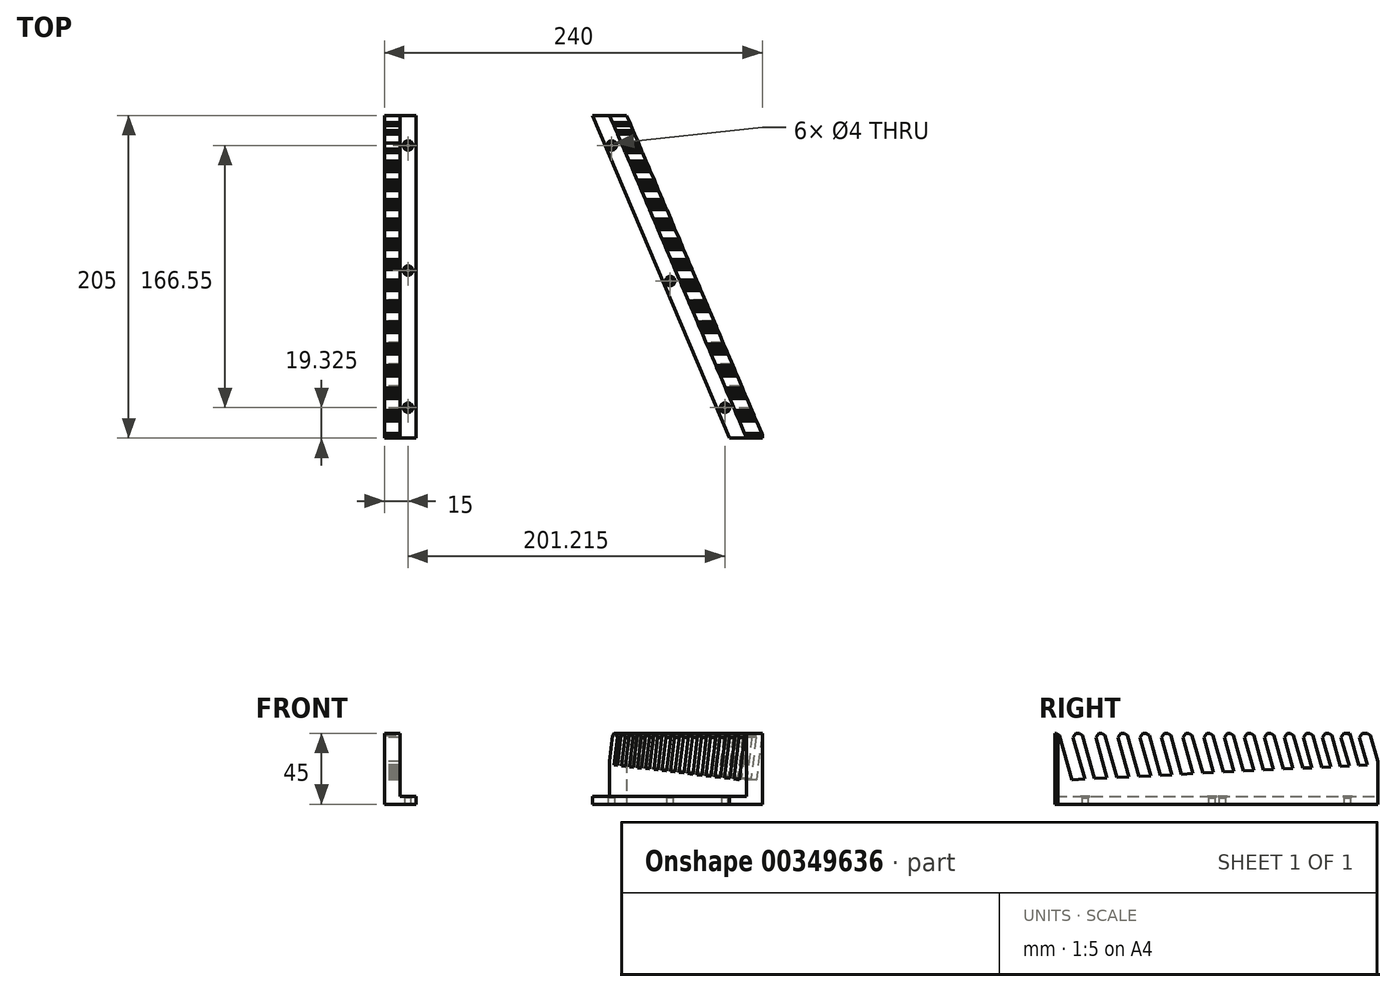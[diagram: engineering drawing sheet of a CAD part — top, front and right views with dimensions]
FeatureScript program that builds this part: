
annotation { "Feature Type Name" : "Feature", "Feature Type Description" : "" }
export const myFeature = defineFeature(function(context is Context, id is Id, definition is map)
    precondition{}
    {
        {
            var Q0;
            Q0=qCreatedBy(makeId("Right.planeOp"),FACE);
            var sketch = newSketch(context, id + "F0", { "sketchPlane" : qUnion([Q0])});
            skLineSegment(sketch, "E0.bottom", {"start": v(0, 0) * mm, "end": v(200, 0) * mm});
            skLineSegment(sketch, "E0.top", {"start": v(0, 45) * mm, "end": v(2.54, 45) * mm});
            skLineSegment(sketch, "E0.left", {"start": v(0, 0) * mm, "end": v(0, 45) * mm});
            skLineSegment(sketch, "E1", {"start": v(198.34, 24.92) * mm, "end": v(193.01, 24.65) * mm});
            skLineSegment(sketch, "E2", {"start": v(2.54, 45) * mm, "end": v(10.85, 15.54) * mm});
            skLineSegment(sketch, "E3", {"start": v(10.85, 45) * mm, "end": v(19.05, 15.95) * mm});
            skLineSegment(sketch, "E4", {"start": v(17.09, 45) * mm, "end": v(25.2, 16.26) * mm});
            skLineSegment(sketch, "E5", {"start": v(25.2, 45) * mm, "end": v(33.3, 16.26) * mm});
            skLineSegment(sketch, "E6", {"start": v(31.43, 45) * mm, "end": v(39.33, 16.97) * mm});
            skLineSegment(sketch, "E7", {"start": v(39.32, 45) * mm, "end": v(47.12, 17.36) * mm});
            skLineSegment(sketch, "E8", {"start": v(45.56, 45) * mm, "end": v(53.27, 17.66) * mm});
            skLineSegment(sketch, "E9", {"start": v(53.25, 45) * mm, "end": v(60.85, 18.04) * mm});
            skLineSegment(sketch, "E10", {"start": v(59.48, 45) * mm, "end": v(67, 18.35) * mm});
            skLineSegment(sketch, "E11", {"start": v(66.96, 45) * mm, "end": v(74.37, 18.72) * mm});
            skLineSegment(sketch, "E12", {"start": v(73.2, 45) * mm, "end": v(80.52, 19.03) * mm});
            skLineSegment(sketch, "E13", {"start": v(80.47, 45) * mm, "end": v(87.69, 19.38) * mm});
            skLineSegment(sketch, "E14", {"start": v(86.7, 45) * mm, "end": v(93.84, 19.7) * mm});
            skLineSegment(sketch, "E15", {"start": v(93.77, 45) * mm, "end": v(100.8, 20.04) * mm});
            skLineSegment(sketch, "E16", {"start": v(100, 45) * mm, "end": v(106.95, 20.35) * mm});
            skLineSegment(sketch, "E17", {"start": v(106.86, 45) * mm, "end": v(113.71, 20.69) * mm});
            skLineSegment(sketch, "E18", {"start": v(113.1, 45) * mm, "end": v(119.86, 21) * mm});
            skLineSegment(sketch, "E19", {"start": v(119.74, 45) * mm, "end": v(126.42, 21.32) * mm});
            skLineSegment(sketch, "E20", {"start": v(125.97, 45) * mm, "end": v(132.57, 21.63) * mm});
            skLineSegment(sketch, "E21", {"start": v(132.42, 45) * mm, "end": v(138.92, 21.95) * mm});
            skLineSegment(sketch, "E22", {"start": v(138.65, 45) * mm, "end": v(145.06, 22.25) * mm});
            skLineSegment(sketch, "E23", {"start": v(144.88, 45) * mm, "end": v(151.21, 22.56) * mm});
            skLineSegment(sketch, "E24", {"start": v(151.12, 45) * mm, "end": v(157.36, 22.87) * mm});
            skLineSegment(sketch, "E25", {"start": v(157.14, 45) * mm, "end": v(163.3, 23.17) * mm});
            skLineSegment(sketch, "E26", {"start": v(163.38, 45) * mm, "end": v(169.45, 23.47) * mm});
            skLineSegment(sketch, "E27", {"start": v(169.2, 45) * mm, "end": v(175.19, 23.76) * mm});
            skLineSegment(sketch, "E28", {"start": v(175.43, 45) * mm, "end": v(181.33, 24.07) * mm});
            skLineSegment(sketch, "E29", {"start": v(181.04, 45) * mm, "end": v(186.87, 24.34) * mm});
            skLineSegment(sketch, "E30", {"start": v(187.28, 45) * mm, "end": v(193.01, 24.65) * mm});
            skLineSegment(sketch, "E31", {"start": v(192.68, 45) * mm, "end": v(198.34, 24.92) * mm});
            skLineSegment(sketch, "E32.trimOffspring", {"start": v(10.85, 45) * mm, "end": v(17.09, 45) * mm});
            skLineSegment(sketch, "E33.trimOffspring", {"start": v(25.2, 45) * mm, "end": v(31.43, 45) * mm});
            skLineSegment(sketch, "E34.trimOffspring", {"start": v(39.32, 45) * mm, "end": v(45.56, 45) * mm});
            skLineSegment(sketch, "E35.trimOffspring", {"start": v(53.25, 45) * mm, "end": v(59.48, 45) * mm});
            skLineSegment(sketch, "E36.trimOffspring", {"start": v(66.96, 45) * mm, "end": v(73.2, 45) * mm});
            skLineSegment(sketch, "E37.trimOffspring", {"start": v(80.47, 45) * mm, "end": v(86.7, 45) * mm});
            skLineSegment(sketch, "E38.trimOffspring", {"start": v(93.77, 45) * mm, "end": v(100, 45) * mm});
            skLineSegment(sketch, "E39.trimOffspring", {"start": v(106.86, 45) * mm, "end": v(113.1, 45) * mm});
            skLineSegment(sketch, "E40.trimOffspring", {"start": v(119.74, 45) * mm, "end": v(125.97, 45) * mm});
            skLineSegment(sketch, "E41.trimOffspring", {"start": v(132.42, 45) * mm, "end": v(138.65, 45) * mm});
            skLineSegment(sketch, "E42.trimOffspring", {"start": v(144.88, 45) * mm, "end": v(151.12, 45) * mm});
            skLineSegment(sketch, "E43.trimOffspring", {"start": v(157.14, 45) * mm, "end": v(163.38, 45) * mm});
            skLineSegment(sketch, "E44.trimOffspring", {"start": v(169.2, 45) * mm, "end": v(175.43, 45) * mm});
            skLineSegment(sketch, "E45.trimOffspring", {"start": v(181.04, 45) * mm, "end": v(187.28, 45) * mm});
            skLineSegment(sketch, "E46.trimOffspring", {"start": v(192.68, 45) * mm, "end": v(200, 45) * mm});
            skLineSegment(sketch, "E47", {"start": v(205, 27.27) * mm, "end": v(205, 0) * mm});
            skLineSegment(sketch, "E48", {"start": v(205, 0) * mm, "end": v(200, 0) * mm});
            skLineSegment(sketch, "E49", {"start": v(200, 45) * mm, "end": v(205, 27.27) * mm});
            skPoint(sketch, "E50.orphan", {"position": v(0, 15) * mm});
            skLineSegment(sketch, "E51.trimOffspring", {"start": v(19.05, 15.95) * mm, "end": v(10.85, 15.54) * mm});
            skLineSegment(sketch, "E52.trimOffspring", {"start": v(33.18, 16.66) * mm, "end": v(25.2, 16.26) * mm});
            skLineSegment(sketch, "E53.trimOffspring", {"start": v(47.12, 17.36) * mm, "end": v(39.33, 16.97) * mm});
            skLineSegment(sketch, "E54.trimOffspring", {"start": v(60.85, 18.04) * mm, "end": v(53.27, 17.66) * mm});
            skLineSegment(sketch, "E55.trimOffspring", {"start": v(74.37, 18.72) * mm, "end": v(67, 18.35) * mm});
            skLineSegment(sketch, "E56.trimOffspring", {"start": v(87.69, 19.38) * mm, "end": v(80.52, 19.03) * mm});
            skLineSegment(sketch, "E57.trimOffspring", {"start": v(100.8, 20.04) * mm, "end": v(93.84, 19.7) * mm});
            skLineSegment(sketch, "E58.trimOffspring", {"start": v(113.71, 20.69) * mm, "end": v(106.95, 20.35) * mm});
            skLineSegment(sketch, "E59.trimOffspring", {"start": v(126.42, 21.32) * mm, "end": v(119.86, 21) * mm});
            skLineSegment(sketch, "E60.trimOffspring", {"start": v(138.92, 21.95) * mm, "end": v(132.57, 21.63) * mm});
            skLineSegment(sketch, "E61.trimOffspring", {"start": v(151.21, 22.56) * mm, "end": v(145.06, 22.25) * mm});
            skLineSegment(sketch, "E62.trimOffspring", {"start": v(163.3, 23.17) * mm, "end": v(157.36, 22.87) * mm});
            skLineSegment(sketch, "E63.trimOffspring", {"start": v(175.19, 23.76) * mm, "end": v(169.45, 23.47) * mm});
            skLineSegment(sketch, "E64.trimOffspring", {"start": v(186.87, 24.34) * mm, "end": v(181.33, 24.07) * mm});
            skSolve(sketch);
        }
        {
            var Q0;
            Q0 = qSketchRegion(id + "F0", true);
            extrude(context, id + "F1", {"entities" : qUnion([Q0]), "depth" : 240 * mm});
        }
        {
            var Q0;
            Q0=makeQuery(id+"F1.opExtrude","SWEPT_FACE",FACE,{"disambiguationData":[OSD([sQuery(id+"F0.wireOp",EDGE,"E32.trimOffspring")])]});
            var sketch = newSketch(context, id + "F2", { "sketchPlane" : qUnion([Q0])});
            skLineSegment(sketch, "E65", {"start": v(10, -4.17) * mm, "end": v(10, 209.1) * mm});
            skLineSegment(sketch, "E66", {"start": v(230, 0) * mm, "end": v(141.25, 209.1) * mm});
            skLineSegment(sketch, "E67", {"start": v(240.86, 0) * mm, "end": v(152.1, 209.1) * mm});
            skLineSegment(sketch, "E68", {"start": v(230, 0) * mm, "end": v(10, 0) * mm});
            skLineSegment(sketch, "E69", {"start": v(240.86, 0) * mm, "end": v(240.86, 209.1) * mm});
            skLineSegment(sketch, "E70", {"start": v(10, 209.1) * mm, "end": v(141.25, 209.1) * mm});
            skLineSegment(sketch, "E71.trimOffspring", {"start": v(152.1, 209.1) * mm, "end": v(240.86, 209.1) * mm});
            skSolve(sketch);
        }
        {
            var Q0;
            Q0 = qSketchRegion(id + "F2", true);
            extrude(context, id + "F3", {"entities" : qUnion([Q0]), "operationType" : NewBodyOperationType.REMOVE, "oppositeDirection" : true, "depth" : 40 * mm});
        }
        {
            var Q0;
            {var subQ0=sQuery(id+"F0.wireOp",EDGE,"E41.trimOffspring");Q0=makeQuery(id+"F3.boolean.opBoolean","SPLIT",FACE,{"disambiguationData":[TD([makeQuery(id+"F3.opExtrude","SWEPT_FACE",FACE,{"disambiguationData":[OSD([sQuery(id+"F2.wireOp",EDGE,"E65")])]})])],"derivedFrom":makeQuery(id+"F1.opExtrude","SWEPT_FACE",FACE,{"disambiguationData":[OSD([subQ0])]})});}
            var sketch = newSketch(context, id + "F4", { "sketchPlane" : qUnion([Q0])});
            skLineSegment(sketch, "E72", {"start": v(20, 206.07) * mm, "end": v(20, 0) * mm});
            skLineSegment(sketch, "E73", {"start": v(131.66, 206.07) * mm, "end": v(219.14, 0) * mm});
            skLineSegment(sketch, "E74", {"start": v(219.14, 0) * mm, "end": v(20, 0) * mm});
            skLineSegment(sketch, "E75", {"start": v(131.66, 206.07) * mm, "end": v(20, 206.07) * mm});
            skCircle(sketch, "E76", {"center": v(15, 185.87) * mm, "radius": 2 * mm});
            skCircle(sketch, "E77", {"center": v(15, 106.48) * mm, "radius": 2 * mm});
            skCircle(sketch, "E78", {"center": v(15, 19.32) * mm, "radius": 2 * mm});
            skCircle(sketch, "E79", {"center": v(144.34, 185.87) * mm, "radius": 2 * mm});
            skCircle(sketch, "E80", {"center": v(181.5, 99.8) * mm, "radius": 2 * mm});
            skCircle(sketch, "E81", {"center": v(216.22, 19.32) * mm, "radius": 2 * mm});
            skLineSegment(sketch, "E82", {"start": v(152.28, 208.7) * mm, "end": v(243.7, -6.68) * mm});
            skLineSegment(sketch, "E83", {"start": v(243.7, -6.68) * mm, "end": v(243.7, 208.7) * mm});
            skLineSegment(sketch, "E84", {"start": v(243.7, 208.7) * mm, "end": v(152.28, 208.7) * mm});
            skSolve(sketch);
        }
        {
            var Q0;
            Q0 = qSketchRegion(id + "F4", true);
            extrude(context, id + "F5", {"entities" : qUnion([Q0]), "operationType" : NewBodyOperationType.REMOVE, "endBound" : BoundingType.THROUGH_ALL, "oppositeDirection" : true, "depth" : 25 * mm});
        }
        {
            var Q0;
            Q0=makeQuery(id+"F5.boolean.opBoolean","INTERSECT",EDGE,{"derivedFrom":[makeQuery(id+"F3.boolean.opBoolean","COPY",FACE,{"derivedFrom":makeQuery(id+"F3.opExtrude","CAP_FACE",FACE,{"disambiguationData":[OSD([sQuery(id+"F2.wireOp",EDGE,"E65"),sQuery(id+"F2.wireOp",EDGE,"E66"),sQuery(id+"F2.wireOp",EDGE,"E68"),sQuery(id+"F2.wireOp",EDGE,"E70")])],"isStart":false})}),makeQuery(id+"F5.opExtrude","SWEPT_FACE",FACE,{"disambiguationData":[OSD([sQuery(id+"F4.wireOp",EDGE,"E76")])]})]});
            var Q1;
            Q1=makeQuery(id+"F5.boolean.opBoolean","INTERSECT",EDGE,{"derivedFrom":[makeQuery(id+"F3.boolean.opBoolean","COPY",FACE,{"derivedFrom":makeQuery(id+"F3.opExtrude","CAP_FACE",FACE,{"disambiguationData":[OSD([sQuery(id+"F2.wireOp",EDGE,"E65"),sQuery(id+"F2.wireOp",EDGE,"E66"),sQuery(id+"F2.wireOp",EDGE,"E68"),sQuery(id+"F2.wireOp",EDGE,"E70")])],"isStart":false})}),makeQuery(id+"F5.opExtrude","SWEPT_FACE",FACE,{"disambiguationData":[OSD([sQuery(id+"F4.wireOp",EDGE,"E77")])]})]});
            var Q2;
            Q2=makeQuery(id+"F5.boolean.opBoolean","INTERSECT",EDGE,{"derivedFrom":[makeQuery(id+"F3.boolean.opBoolean","COPY",FACE,{"derivedFrom":makeQuery(id+"F3.opExtrude","CAP_FACE",FACE,{"disambiguationData":[OSD([sQuery(id+"F2.wireOp",EDGE,"E65"),sQuery(id+"F2.wireOp",EDGE,"E66"),sQuery(id+"F2.wireOp",EDGE,"E68"),sQuery(id+"F2.wireOp",EDGE,"E70")])],"isStart":false})}),makeQuery(id+"F5.opExtrude","SWEPT_FACE",FACE,{"disambiguationData":[OSD([sQuery(id+"F4.wireOp",EDGE,"E78")])]})]});
            var Q3;
            Q3=makeQuery(id+"F5.boolean.opBoolean","INTERSECT",EDGE,{"derivedFrom":[makeQuery(id+"F3.boolean.opBoolean","COPY",FACE,{"derivedFrom":makeQuery(id+"F3.opExtrude","CAP_FACE",FACE,{"disambiguationData":[OSD([sQuery(id+"F2.wireOp",EDGE,"E65"),sQuery(id+"F2.wireOp",EDGE,"E66"),sQuery(id+"F2.wireOp",EDGE,"E68"),sQuery(id+"F2.wireOp",EDGE,"E70")])],"isStart":false})}),makeQuery(id+"F5.opExtrude","SWEPT_FACE",FACE,{"disambiguationData":[OSD([sQuery(id+"F4.wireOp",EDGE,"E81")])]})]});
            var Q4;
            Q4=makeQuery(id+"F5.boolean.opBoolean","INTERSECT",EDGE,{"derivedFrom":[makeQuery(id+"F3.boolean.opBoolean","COPY",FACE,{"derivedFrom":makeQuery(id+"F3.opExtrude","CAP_FACE",FACE,{"disambiguationData":[OSD([sQuery(id+"F2.wireOp",EDGE,"E65"),sQuery(id+"F2.wireOp",EDGE,"E66"),sQuery(id+"F2.wireOp",EDGE,"E68"),sQuery(id+"F2.wireOp",EDGE,"E70")])],"isStart":false})}),makeQuery(id+"F5.opExtrude","SWEPT_FACE",FACE,{"disambiguationData":[OSD([sQuery(id+"F4.wireOp",EDGE,"E80")])]})]});
            var Q5;
            Q5=makeQuery(id+"F5.boolean.opBoolean","INTERSECT",EDGE,{"derivedFrom":[makeQuery(id+"F3.boolean.opBoolean","COPY",FACE,{"derivedFrom":makeQuery(id+"F3.opExtrude","CAP_FACE",FACE,{"disambiguationData":[OSD([sQuery(id+"F2.wireOp",EDGE,"E65"),sQuery(id+"F2.wireOp",EDGE,"E66"),sQuery(id+"F2.wireOp",EDGE,"E68"),sQuery(id+"F2.wireOp",EDGE,"E70")])],"isStart":false})}),makeQuery(id+"F5.opExtrude","SWEPT_FACE",FACE,{"disambiguationData":[OSD([sQuery(id+"F4.wireOp",EDGE,"E79")])]})]});
            chamfer(context, id + "F6", {"entities" : qUnion([Q0, Q1, Q2, Q3, Q4, Q5]), "width" : 1 * mm, "tangentPropagation" : true});
        }
        {
            var Q0;
            {var subQ0=sQuery(id+"F0.wireOp",EDGE,"E46.trimOffspring");var subQ1=sQuery(id+"F0.wireOp",EDGE,"E49");Q0=makeQuery(id+"F3.boolean.opBoolean","SPLIT",EDGE,{"disambiguationData":[TD([makeQuery(id+"F3.opExtrude","SWEPT_FACE",FACE,{"disambiguationData":[OSD([sQuery(id+"F2.wireOp",EDGE,"E66")])]})])],"derivedFrom":makeQuery(id+"F1.opExtrude","SWEPT_EDGE",EDGE,{"disambiguationData":[OSD([subQ0,subQ1])]})});}
            var Q1;
            {var subQ0=sQuery(id+"F0.wireOp",EDGE,"E31");var subQ1=sQuery(id+"F0.wireOp",EDGE,"E46.trimOffspring");Q1=makeQuery(id+"F3.boolean.opBoolean","SPLIT",EDGE,{"disambiguationData":[TD([makeQuery(id+"F3.opExtrude","SWEPT_FACE",FACE,{"disambiguationData":[OSD([sQuery(id+"F2.wireOp",EDGE,"E66")])]})])],"derivedFrom":makeQuery(id+"F1.opExtrude","SWEPT_EDGE",EDGE,{"disambiguationData":[OSD([subQ0,subQ1])]})});}
            var Q2;
            {var subQ0=sQuery(id+"F0.wireOp",EDGE,"E30");var subQ1=sQuery(id+"F0.wireOp",EDGE,"E45.trimOffspring");Q2=makeQuery(id+"F3.boolean.opBoolean","SPLIT",EDGE,{"disambiguationData":[TD([makeQuery(id+"F3.opExtrude","SWEPT_FACE",FACE,{"disambiguationData":[OSD([sQuery(id+"F2.wireOp",EDGE,"E66")])]})])],"derivedFrom":makeQuery(id+"F1.opExtrude","SWEPT_EDGE",EDGE,{"disambiguationData":[OSD([subQ0,subQ1])]})});}
            var Q3;
            {var subQ0=sQuery(id+"F0.wireOp",EDGE,"E29");var subQ1=sQuery(id+"F0.wireOp",EDGE,"E45.trimOffspring");Q3=makeQuery(id+"F3.boolean.opBoolean","SPLIT",EDGE,{"disambiguationData":[TD([makeQuery(id+"F3.opExtrude","SWEPT_FACE",FACE,{"disambiguationData":[OSD([sQuery(id+"F2.wireOp",EDGE,"E66")])]})])],"derivedFrom":makeQuery(id+"F1.opExtrude","SWEPT_EDGE",EDGE,{"disambiguationData":[OSD([subQ0,subQ1])]})});}
            var Q4;
            {var subQ0=sQuery(id+"F0.wireOp",EDGE,"E28");var subQ1=sQuery(id+"F0.wireOp",EDGE,"E44.trimOffspring");Q4=makeQuery(id+"F3.boolean.opBoolean","SPLIT",EDGE,{"disambiguationData":[TD([makeQuery(id+"F3.opExtrude","SWEPT_FACE",FACE,{"disambiguationData":[OSD([sQuery(id+"F2.wireOp",EDGE,"E66")])]})])],"derivedFrom":makeQuery(id+"F1.opExtrude","SWEPT_EDGE",EDGE,{"disambiguationData":[OSD([subQ0,subQ1])]})});}
            var Q5;
            {var subQ0=sQuery(id+"F0.wireOp",EDGE,"E27");var subQ1=sQuery(id+"F0.wireOp",EDGE,"E44.trimOffspring");Q5=makeQuery(id+"F3.boolean.opBoolean","SPLIT",EDGE,{"disambiguationData":[TD([makeQuery(id+"F3.opExtrude","SWEPT_FACE",FACE,{"disambiguationData":[OSD([sQuery(id+"F2.wireOp",EDGE,"E66")])]})])],"derivedFrom":makeQuery(id+"F1.opExtrude","SWEPT_EDGE",EDGE,{"disambiguationData":[OSD([subQ0,subQ1])]})});}
            var Q6;
            {var subQ0=sQuery(id+"F0.wireOp",EDGE,"E26");var subQ1=sQuery(id+"F0.wireOp",EDGE,"E43.trimOffspring");Q6=makeQuery(id+"F3.boolean.opBoolean","SPLIT",EDGE,{"disambiguationData":[TD([makeQuery(id+"F3.opExtrude","SWEPT_FACE",FACE,{"disambiguationData":[OSD([sQuery(id+"F2.wireOp",EDGE,"E66")])]})])],"derivedFrom":makeQuery(id+"F1.opExtrude","SWEPT_EDGE",EDGE,{"disambiguationData":[OSD([subQ0,subQ1])]})});}
            var Q7;
            {var subQ0=sQuery(id+"F0.wireOp",EDGE,"E25");var subQ1=sQuery(id+"F0.wireOp",EDGE,"E43.trimOffspring");Q7=makeQuery(id+"F3.boolean.opBoolean","SPLIT",EDGE,{"disambiguationData":[TD([makeQuery(id+"F3.opExtrude","SWEPT_FACE",FACE,{"disambiguationData":[OSD([sQuery(id+"F2.wireOp",EDGE,"E66")])]})])],"derivedFrom":makeQuery(id+"F1.opExtrude","SWEPT_EDGE",EDGE,{"disambiguationData":[OSD([subQ0,subQ1])]})});}
            var Q8;
            {var subQ0=sQuery(id+"F0.wireOp",EDGE,"E24");var subQ1=sQuery(id+"F0.wireOp",EDGE,"E42.trimOffspring");Q8=makeQuery(id+"F3.boolean.opBoolean","SPLIT",EDGE,{"disambiguationData":[TD([makeQuery(id+"F3.opExtrude","SWEPT_FACE",FACE,{"disambiguationData":[OSD([sQuery(id+"F2.wireOp",EDGE,"E66")])]})])],"derivedFrom":makeQuery(id+"F1.opExtrude","SWEPT_EDGE",EDGE,{"disambiguationData":[OSD([subQ0,subQ1])]})});}
            var Q9;
            {var subQ0=sQuery(id+"F0.wireOp",EDGE,"E23");var subQ1=sQuery(id+"F0.wireOp",EDGE,"E42.trimOffspring");Q9=makeQuery(id+"F3.boolean.opBoolean","SPLIT",EDGE,{"disambiguationData":[TD([makeQuery(id+"F3.opExtrude","SWEPT_FACE",FACE,{"disambiguationData":[OSD([sQuery(id+"F2.wireOp",EDGE,"E66")])]})])],"derivedFrom":makeQuery(id+"F1.opExtrude","SWEPT_EDGE",EDGE,{"disambiguationData":[OSD([subQ0,subQ1])]})});}
            var Q10;
            {var subQ0=sQuery(id+"F0.wireOp",EDGE,"E22");var subQ1=sQuery(id+"F0.wireOp",EDGE,"E41.trimOffspring");Q10=makeQuery(id+"F3.boolean.opBoolean","SPLIT",EDGE,{"disambiguationData":[TD([makeQuery(id+"F3.opExtrude","SWEPT_FACE",FACE,{"disambiguationData":[OSD([sQuery(id+"F2.wireOp",EDGE,"E66")])]})])],"derivedFrom":makeQuery(id+"F1.opExtrude","SWEPT_EDGE",EDGE,{"disambiguationData":[OSD([subQ0,subQ1])]})});}
            var Q11;
            {var subQ0=sQuery(id+"F0.wireOp",EDGE,"E21");var subQ1=sQuery(id+"F0.wireOp",EDGE,"E41.trimOffspring");Q11=makeQuery(id+"F3.boolean.opBoolean","SPLIT",EDGE,{"disambiguationData":[TD([makeQuery(id+"F3.opExtrude","SWEPT_FACE",FACE,{"disambiguationData":[OSD([sQuery(id+"F2.wireOp",EDGE,"E66")])]})])],"derivedFrom":makeQuery(id+"F1.opExtrude","SWEPT_EDGE",EDGE,{"disambiguationData":[OSD([subQ0,subQ1])]})});}
            var Q12;
            {var subQ0=sQuery(id+"F0.wireOp",EDGE,"E20");var subQ1=sQuery(id+"F0.wireOp",EDGE,"E40.trimOffspring");Q12=makeQuery(id+"F3.boolean.opBoolean","SPLIT",EDGE,{"disambiguationData":[TD([makeQuery(id+"F3.opExtrude","SWEPT_FACE",FACE,{"disambiguationData":[OSD([sQuery(id+"F2.wireOp",EDGE,"E66")])]})])],"derivedFrom":makeQuery(id+"F1.opExtrude","SWEPT_EDGE",EDGE,{"disambiguationData":[OSD([subQ0,subQ1])]})});}
            var Q13;
            {var subQ0=sQuery(id+"F0.wireOp",EDGE,"E19");var subQ1=sQuery(id+"F0.wireOp",EDGE,"E40.trimOffspring");Q13=makeQuery(id+"F3.boolean.opBoolean","SPLIT",EDGE,{"disambiguationData":[TD([makeQuery(id+"F3.opExtrude","SWEPT_FACE",FACE,{"disambiguationData":[OSD([sQuery(id+"F2.wireOp",EDGE,"E66")])]})])],"derivedFrom":makeQuery(id+"F1.opExtrude","SWEPT_EDGE",EDGE,{"disambiguationData":[OSD([subQ0,subQ1])]})});}
            var Q14;
            {var subQ0=sQuery(id+"F0.wireOp",EDGE,"E18");var subQ1=sQuery(id+"F0.wireOp",EDGE,"E39.trimOffspring");Q14=makeQuery(id+"F3.boolean.opBoolean","SPLIT",EDGE,{"disambiguationData":[TD([makeQuery(id+"F3.opExtrude","SWEPT_FACE",FACE,{"disambiguationData":[OSD([sQuery(id+"F2.wireOp",EDGE,"E66")])]})])],"derivedFrom":makeQuery(id+"F1.opExtrude","SWEPT_EDGE",EDGE,{"disambiguationData":[OSD([subQ0,subQ1])]})});}
            var Q15;
            {var subQ0=sQuery(id+"F0.wireOp",EDGE,"E17");var subQ1=sQuery(id+"F0.wireOp",EDGE,"E39.trimOffspring");Q15=makeQuery(id+"F3.boolean.opBoolean","SPLIT",EDGE,{"disambiguationData":[TD([makeQuery(id+"F3.opExtrude","SWEPT_FACE",FACE,{"disambiguationData":[OSD([sQuery(id+"F2.wireOp",EDGE,"E66")])]})])],"derivedFrom":makeQuery(id+"F1.opExtrude","SWEPT_EDGE",EDGE,{"disambiguationData":[OSD([subQ0,subQ1])]})});}
            var Q16;
            {var subQ0=sQuery(id+"F0.wireOp",EDGE,"E16");var subQ1=sQuery(id+"F0.wireOp",EDGE,"E38.trimOffspring");Q16=makeQuery(id+"F3.boolean.opBoolean","SPLIT",EDGE,{"disambiguationData":[TD([makeQuery(id+"F3.opExtrude","SWEPT_FACE",FACE,{"disambiguationData":[OSD([sQuery(id+"F2.wireOp",EDGE,"E66")])]})])],"derivedFrom":makeQuery(id+"F1.opExtrude","SWEPT_EDGE",EDGE,{"disambiguationData":[OSD([subQ0,subQ1])]})});}
            var Q17;
            {var subQ0=sQuery(id+"F0.wireOp",EDGE,"E15");var subQ1=sQuery(id+"F0.wireOp",EDGE,"E38.trimOffspring");Q17=makeQuery(id+"F3.boolean.opBoolean","SPLIT",EDGE,{"disambiguationData":[TD([makeQuery(id+"F3.opExtrude","SWEPT_FACE",FACE,{"disambiguationData":[OSD([sQuery(id+"F2.wireOp",EDGE,"E66")])]})])],"derivedFrom":makeQuery(id+"F1.opExtrude","SWEPT_EDGE",EDGE,{"disambiguationData":[OSD([subQ0,subQ1])]})});}
            var Q18;
            {var subQ0=sQuery(id+"F0.wireOp",EDGE,"E14");var subQ1=sQuery(id+"F0.wireOp",EDGE,"E37.trimOffspring");Q18=makeQuery(id+"F3.boolean.opBoolean","SPLIT",EDGE,{"disambiguationData":[TD([makeQuery(id+"F3.opExtrude","SWEPT_FACE",FACE,{"disambiguationData":[OSD([sQuery(id+"F2.wireOp",EDGE,"E66")])]})])],"derivedFrom":makeQuery(id+"F1.opExtrude","SWEPT_EDGE",EDGE,{"disambiguationData":[OSD([subQ0,subQ1])]})});}
            var Q19;
            {var subQ0=sQuery(id+"F0.wireOp",EDGE,"E13");var subQ1=sQuery(id+"F0.wireOp",EDGE,"E37.trimOffspring");Q19=makeQuery(id+"F3.boolean.opBoolean","SPLIT",EDGE,{"disambiguationData":[TD([makeQuery(id+"F3.opExtrude","SWEPT_FACE",FACE,{"disambiguationData":[OSD([sQuery(id+"F2.wireOp",EDGE,"E66")])]})])],"derivedFrom":makeQuery(id+"F1.opExtrude","SWEPT_EDGE",EDGE,{"disambiguationData":[OSD([subQ0,subQ1])]})});}
            var Q20;
            {var subQ0=sQuery(id+"F0.wireOp",EDGE,"E12");var subQ1=sQuery(id+"F0.wireOp",EDGE,"E36.trimOffspring");Q20=makeQuery(id+"F3.boolean.opBoolean","SPLIT",EDGE,{"disambiguationData":[TD([makeQuery(id+"F3.opExtrude","SWEPT_FACE",FACE,{"disambiguationData":[OSD([sQuery(id+"F2.wireOp",EDGE,"E66")])]})])],"derivedFrom":makeQuery(id+"F1.opExtrude","SWEPT_EDGE",EDGE,{"disambiguationData":[OSD([subQ0,subQ1])]})});}
            var Q21;
            {var subQ0=sQuery(id+"F0.wireOp",EDGE,"E11");var subQ1=sQuery(id+"F0.wireOp",EDGE,"E36.trimOffspring");Q21=makeQuery(id+"F3.boolean.opBoolean","SPLIT",EDGE,{"disambiguationData":[TD([makeQuery(id+"F3.opExtrude","SWEPT_FACE",FACE,{"disambiguationData":[OSD([sQuery(id+"F2.wireOp",EDGE,"E66")])]})])],"derivedFrom":makeQuery(id+"F1.opExtrude","SWEPT_EDGE",EDGE,{"disambiguationData":[OSD([subQ0,subQ1])]})});}
            var Q22;
            {var subQ0=sQuery(id+"F0.wireOp",EDGE,"E10");var subQ1=sQuery(id+"F0.wireOp",EDGE,"E35.trimOffspring");Q22=makeQuery(id+"F3.boolean.opBoolean","SPLIT",EDGE,{"disambiguationData":[TD([makeQuery(id+"F3.opExtrude","SWEPT_FACE",FACE,{"disambiguationData":[OSD([sQuery(id+"F2.wireOp",EDGE,"E66")])]})])],"derivedFrom":makeQuery(id+"F1.opExtrude","SWEPT_EDGE",EDGE,{"disambiguationData":[OSD([subQ0,subQ1])]})});}
            var Q23;
            {var subQ0=sQuery(id+"F0.wireOp",EDGE,"E9");var subQ1=sQuery(id+"F0.wireOp",EDGE,"E35.trimOffspring");Q23=makeQuery(id+"F3.boolean.opBoolean","SPLIT",EDGE,{"disambiguationData":[TD([makeQuery(id+"F3.opExtrude","SWEPT_FACE",FACE,{"disambiguationData":[OSD([sQuery(id+"F2.wireOp",EDGE,"E66")])]})])],"derivedFrom":makeQuery(id+"F1.opExtrude","SWEPT_EDGE",EDGE,{"disambiguationData":[OSD([subQ0,subQ1])]})});}
            var Q24;
            {var subQ0=sQuery(id+"F0.wireOp",EDGE,"E8");var subQ1=sQuery(id+"F0.wireOp",EDGE,"E34.trimOffspring");Q24=makeQuery(id+"F3.boolean.opBoolean","SPLIT",EDGE,{"disambiguationData":[TD([makeQuery(id+"F3.opExtrude","SWEPT_FACE",FACE,{"disambiguationData":[OSD([sQuery(id+"F2.wireOp",EDGE,"E66")])]})])],"derivedFrom":makeQuery(id+"F1.opExtrude","SWEPT_EDGE",EDGE,{"disambiguationData":[OSD([subQ0,subQ1])]})});}
            var Q25;
            {var subQ0=sQuery(id+"F0.wireOp",EDGE,"E7");var subQ1=sQuery(id+"F0.wireOp",EDGE,"E34.trimOffspring");Q25=makeQuery(id+"F3.boolean.opBoolean","SPLIT",EDGE,{"disambiguationData":[TD([makeQuery(id+"F3.opExtrude","SWEPT_FACE",FACE,{"disambiguationData":[OSD([sQuery(id+"F2.wireOp",EDGE,"E66")])]})])],"derivedFrom":makeQuery(id+"F1.opExtrude","SWEPT_EDGE",EDGE,{"disambiguationData":[OSD([subQ0,subQ1])]})});}
            var Q26;
            {var subQ0=sQuery(id+"F0.wireOp",EDGE,"E6");var subQ1=sQuery(id+"F0.wireOp",EDGE,"E33.trimOffspring");Q26=makeQuery(id+"F3.boolean.opBoolean","SPLIT",EDGE,{"disambiguationData":[TD([makeQuery(id+"F3.opExtrude","SWEPT_FACE",FACE,{"disambiguationData":[OSD([sQuery(id+"F2.wireOp",EDGE,"E66")])]})])],"derivedFrom":makeQuery(id+"F1.opExtrude","SWEPT_EDGE",EDGE,{"disambiguationData":[OSD([subQ0,subQ1])]})});}
            var Q27;
            {var subQ0=sQuery(id+"F0.wireOp",EDGE,"E5");var subQ1=sQuery(id+"F0.wireOp",EDGE,"E33.trimOffspring");Q27=makeQuery(id+"F3.boolean.opBoolean","SPLIT",EDGE,{"disambiguationData":[TD([makeQuery(id+"F3.opExtrude","SWEPT_FACE",FACE,{"disambiguationData":[OSD([sQuery(id+"F2.wireOp",EDGE,"E66")])]})])],"derivedFrom":makeQuery(id+"F1.opExtrude","SWEPT_EDGE",EDGE,{"disambiguationData":[OSD([subQ0,subQ1])]})});}
            var Q28;
            {var subQ0=sQuery(id+"F0.wireOp",EDGE,"E4");var subQ1=sQuery(id+"F0.wireOp",EDGE,"E32.trimOffspring");Q28=makeQuery(id+"F3.boolean.opBoolean","SPLIT",EDGE,{"disambiguationData":[TD([makeQuery(id+"F3.opExtrude","SWEPT_FACE",FACE,{"disambiguationData":[OSD([sQuery(id+"F2.wireOp",EDGE,"E66")])]})])],"derivedFrom":makeQuery(id+"F1.opExtrude","SWEPT_EDGE",EDGE,{"disambiguationData":[OSD([subQ0,subQ1])]})});}
            var Q29;
            {var subQ0=sQuery(id+"F0.wireOp",EDGE,"E3");var subQ1=sQuery(id+"F0.wireOp",EDGE,"E32.trimOffspring");Q29=makeQuery(id+"F3.boolean.opBoolean","SPLIT",EDGE,{"disambiguationData":[TD([makeQuery(id+"F3.opExtrude","SWEPT_FACE",FACE,{"disambiguationData":[OSD([sQuery(id+"F2.wireOp",EDGE,"E66")])]})])],"derivedFrom":makeQuery(id+"F1.opExtrude","SWEPT_EDGE",EDGE,{"disambiguationData":[OSD([subQ0,subQ1])]})});}
            var Q30;
            {var subQ0=sQuery(id+"F0.wireOp",EDGE,"E0.top");var subQ1=sQuery(id+"F0.wireOp",EDGE,"E2");Q30=makeQuery(id+"F3.boolean.opBoolean","SPLIT",EDGE,{"disambiguationData":[TD([makeQuery(id+"F3.opExtrude","SWEPT_FACE",FACE,{"disambiguationData":[OSD([sQuery(id+"F2.wireOp",EDGE,"E66")])]})])],"derivedFrom":makeQuery(id+"F1.opExtrude","SWEPT_EDGE",EDGE,{"disambiguationData":[OSD([subQ0,subQ1])]})});}
            var Q31;
            {var subQ0=sQuery(id+"F0.wireOp",EDGE,"E49");var subQ1=sQuery(id+"F0.wireOp",EDGE,"E46.trimOffspring");Q31=makeQuery(id+"F3.boolean.opBoolean","SPLIT",EDGE,{"disambiguationData":[TD([makeQuery(id+"F3.opExtrude","SWEPT_FACE",FACE,{"disambiguationData":[OSD([sQuery(id+"F2.wireOp",EDGE,"E65")])]})])],"derivedFrom":makeQuery(id+"F1.opExtrude","SWEPT_EDGE",EDGE,{"disambiguationData":[OSD([subQ1,subQ0])]})});}
            var Q32;
            {var subQ0=sQuery(id+"F0.wireOp",EDGE,"E46.trimOffspring");var subQ1=sQuery(id+"F0.wireOp",EDGE,"E31");Q32=makeQuery(id+"F3.boolean.opBoolean","SPLIT",EDGE,{"disambiguationData":[TD([makeQuery(id+"F3.opExtrude","SWEPT_FACE",FACE,{"disambiguationData":[OSD([sQuery(id+"F2.wireOp",EDGE,"E65")])]})])],"derivedFrom":makeQuery(id+"F1.opExtrude","SWEPT_EDGE",EDGE,{"disambiguationData":[OSD([subQ1,subQ0])]})});}
            var Q33;
            {var subQ0=sQuery(id+"F0.wireOp",EDGE,"E45.trimOffspring");var subQ1=sQuery(id+"F0.wireOp",EDGE,"E29");Q33=makeQuery(id+"F3.boolean.opBoolean","SPLIT",EDGE,{"disambiguationData":[TD([makeQuery(id+"F3.opExtrude","SWEPT_FACE",FACE,{"disambiguationData":[OSD([sQuery(id+"F2.wireOp",EDGE,"E65")])]})])],"derivedFrom":makeQuery(id+"F1.opExtrude","SWEPT_EDGE",EDGE,{"disambiguationData":[OSD([subQ1,subQ0])]})});}
            var Q34;
            {var subQ0=sQuery(id+"F0.wireOp",EDGE,"E44.trimOffspring");var subQ1=sQuery(id+"F0.wireOp",EDGE,"E28");Q34=makeQuery(id+"F3.boolean.opBoolean","SPLIT",EDGE,{"disambiguationData":[TD([makeQuery(id+"F3.opExtrude","SWEPT_FACE",FACE,{"disambiguationData":[OSD([sQuery(id+"F2.wireOp",EDGE,"E65")])]})])],"derivedFrom":makeQuery(id+"F1.opExtrude","SWEPT_EDGE",EDGE,{"disambiguationData":[OSD([subQ1,subQ0])]})});}
            var Q35;
            {var subQ0=sQuery(id+"F0.wireOp",EDGE,"E44.trimOffspring");var subQ1=sQuery(id+"F0.wireOp",EDGE,"E27");Q35=makeQuery(id+"F3.boolean.opBoolean","SPLIT",EDGE,{"disambiguationData":[TD([makeQuery(id+"F3.opExtrude","SWEPT_FACE",FACE,{"disambiguationData":[OSD([sQuery(id+"F2.wireOp",EDGE,"E65")])]})])],"derivedFrom":makeQuery(id+"F1.opExtrude","SWEPT_EDGE",EDGE,{"disambiguationData":[OSD([subQ1,subQ0])]})});}
            var Q36;
            {var subQ0=sQuery(id+"F0.wireOp",EDGE,"E43.trimOffspring");var subQ1=sQuery(id+"F0.wireOp",EDGE,"E26");Q36=makeQuery(id+"F3.boolean.opBoolean","SPLIT",EDGE,{"disambiguationData":[TD([makeQuery(id+"F3.opExtrude","SWEPT_FACE",FACE,{"disambiguationData":[OSD([sQuery(id+"F2.wireOp",EDGE,"E65")])]})])],"derivedFrom":makeQuery(id+"F1.opExtrude","SWEPT_EDGE",EDGE,{"disambiguationData":[OSD([subQ1,subQ0])]})});}
            var Q37;
            {var subQ0=sQuery(id+"F0.wireOp",EDGE,"E43.trimOffspring");var subQ1=sQuery(id+"F0.wireOp",EDGE,"E25");Q37=makeQuery(id+"F3.boolean.opBoolean","SPLIT",EDGE,{"disambiguationData":[TD([makeQuery(id+"F3.opExtrude","SWEPT_FACE",FACE,{"disambiguationData":[OSD([sQuery(id+"F2.wireOp",EDGE,"E65")])]})])],"derivedFrom":makeQuery(id+"F1.opExtrude","SWEPT_EDGE",EDGE,{"disambiguationData":[OSD([subQ1,subQ0])]})});}
            var Q38;
            {var subQ0=sQuery(id+"F0.wireOp",EDGE,"E42.trimOffspring");var subQ1=sQuery(id+"F0.wireOp",EDGE,"E24");Q38=makeQuery(id+"F3.boolean.opBoolean","SPLIT",EDGE,{"disambiguationData":[TD([makeQuery(id+"F3.opExtrude","SWEPT_FACE",FACE,{"disambiguationData":[OSD([sQuery(id+"F2.wireOp",EDGE,"E65")])]})])],"derivedFrom":makeQuery(id+"F1.opExtrude","SWEPT_EDGE",EDGE,{"disambiguationData":[OSD([subQ1,subQ0])]})});}
            var Q39;
            {var subQ0=sQuery(id+"F0.wireOp",EDGE,"E42.trimOffspring");var subQ1=sQuery(id+"F0.wireOp",EDGE,"E23");Q39=makeQuery(id+"F3.boolean.opBoolean","SPLIT",EDGE,{"disambiguationData":[TD([makeQuery(id+"F3.opExtrude","SWEPT_FACE",FACE,{"disambiguationData":[OSD([sQuery(id+"F2.wireOp",EDGE,"E65")])]})])],"derivedFrom":makeQuery(id+"F1.opExtrude","SWEPT_EDGE",EDGE,{"disambiguationData":[OSD([subQ1,subQ0])]})});}
            var Q40;
            {var subQ0=sQuery(id+"F0.wireOp",EDGE,"E41.trimOffspring");var subQ1=sQuery(id+"F0.wireOp",EDGE,"E22");Q40=makeQuery(id+"F3.boolean.opBoolean","SPLIT",EDGE,{"disambiguationData":[TD([makeQuery(id+"F3.opExtrude","SWEPT_FACE",FACE,{"disambiguationData":[OSD([sQuery(id+"F2.wireOp",EDGE,"E65")])]})])],"derivedFrom":makeQuery(id+"F1.opExtrude","SWEPT_EDGE",EDGE,{"disambiguationData":[OSD([subQ1,subQ0])]})});}
            var Q41;
            {var subQ0=sQuery(id+"F0.wireOp",EDGE,"E41.trimOffspring");var subQ1=sQuery(id+"F0.wireOp",EDGE,"E21");Q41=makeQuery(id+"F3.boolean.opBoolean","SPLIT",EDGE,{"disambiguationData":[TD([makeQuery(id+"F3.opExtrude","SWEPT_FACE",FACE,{"disambiguationData":[OSD([sQuery(id+"F2.wireOp",EDGE,"E65")])]})])],"derivedFrom":makeQuery(id+"F1.opExtrude","SWEPT_EDGE",EDGE,{"disambiguationData":[OSD([subQ1,subQ0])]})});}
            var Q42;
            {var subQ0=sQuery(id+"F0.wireOp",EDGE,"E40.trimOffspring");var subQ1=sQuery(id+"F0.wireOp",EDGE,"E20");Q42=makeQuery(id+"F3.boolean.opBoolean","SPLIT",EDGE,{"disambiguationData":[TD([makeQuery(id+"F3.opExtrude","SWEPT_FACE",FACE,{"disambiguationData":[OSD([sQuery(id+"F2.wireOp",EDGE,"E65")])]})])],"derivedFrom":makeQuery(id+"F1.opExtrude","SWEPT_EDGE",EDGE,{"disambiguationData":[OSD([subQ1,subQ0])]})});}
            var Q43;
            {var subQ0=sQuery(id+"F0.wireOp",EDGE,"E40.trimOffspring");var subQ1=sQuery(id+"F0.wireOp",EDGE,"E19");Q43=makeQuery(id+"F3.boolean.opBoolean","SPLIT",EDGE,{"disambiguationData":[TD([makeQuery(id+"F3.opExtrude","SWEPT_FACE",FACE,{"disambiguationData":[OSD([sQuery(id+"F2.wireOp",EDGE,"E65")])]})])],"derivedFrom":makeQuery(id+"F1.opExtrude","SWEPT_EDGE",EDGE,{"disambiguationData":[OSD([subQ1,subQ0])]})});}
            var Q44;
            {var subQ0=sQuery(id+"F0.wireOp",EDGE,"E39.trimOffspring");var subQ1=sQuery(id+"F0.wireOp",EDGE,"E18");Q44=makeQuery(id+"F3.boolean.opBoolean","SPLIT",EDGE,{"disambiguationData":[TD([makeQuery(id+"F3.opExtrude","SWEPT_FACE",FACE,{"disambiguationData":[OSD([sQuery(id+"F2.wireOp",EDGE,"E65")])]})])],"derivedFrom":makeQuery(id+"F1.opExtrude","SWEPT_EDGE",EDGE,{"disambiguationData":[OSD([subQ1,subQ0])]})});}
            var Q45;
            {var subQ0=sQuery(id+"F0.wireOp",EDGE,"E39.trimOffspring");var subQ1=sQuery(id+"F0.wireOp",EDGE,"E17");Q45=makeQuery(id+"F3.boolean.opBoolean","SPLIT",EDGE,{"disambiguationData":[TD([makeQuery(id+"F3.opExtrude","SWEPT_FACE",FACE,{"disambiguationData":[OSD([sQuery(id+"F2.wireOp",EDGE,"E65")])]})])],"derivedFrom":makeQuery(id+"F1.opExtrude","SWEPT_EDGE",EDGE,{"disambiguationData":[OSD([subQ1,subQ0])]})});}
            var Q46;
            {var subQ0=sQuery(id+"F0.wireOp",EDGE,"E38.trimOffspring");var subQ1=sQuery(id+"F0.wireOp",EDGE,"E16");Q46=makeQuery(id+"F3.boolean.opBoolean","SPLIT",EDGE,{"disambiguationData":[TD([makeQuery(id+"F3.opExtrude","SWEPT_FACE",FACE,{"disambiguationData":[OSD([sQuery(id+"F2.wireOp",EDGE,"E65")])]})])],"derivedFrom":makeQuery(id+"F1.opExtrude","SWEPT_EDGE",EDGE,{"disambiguationData":[OSD([subQ1,subQ0])]})});}
            var Q47;
            {var subQ0=sQuery(id+"F0.wireOp",EDGE,"E38.trimOffspring");var subQ1=sQuery(id+"F0.wireOp",EDGE,"E15");Q47=makeQuery(id+"F3.boolean.opBoolean","SPLIT",EDGE,{"disambiguationData":[TD([makeQuery(id+"F3.opExtrude","SWEPT_FACE",FACE,{"disambiguationData":[OSD([sQuery(id+"F2.wireOp",EDGE,"E65")])]})])],"derivedFrom":makeQuery(id+"F1.opExtrude","SWEPT_EDGE",EDGE,{"disambiguationData":[OSD([subQ1,subQ0])]})});}
            var Q48;
            {var subQ0=sQuery(id+"F0.wireOp",EDGE,"E37.trimOffspring");var subQ1=sQuery(id+"F0.wireOp",EDGE,"E14");Q48=makeQuery(id+"F3.boolean.opBoolean","SPLIT",EDGE,{"disambiguationData":[TD([makeQuery(id+"F3.opExtrude","SWEPT_FACE",FACE,{"disambiguationData":[OSD([sQuery(id+"F2.wireOp",EDGE,"E65")])]})])],"derivedFrom":makeQuery(id+"F1.opExtrude","SWEPT_EDGE",EDGE,{"disambiguationData":[OSD([subQ1,subQ0])]})});}
            var Q49;
            {var subQ0=sQuery(id+"F0.wireOp",EDGE,"E37.trimOffspring");var subQ1=sQuery(id+"F0.wireOp",EDGE,"E13");Q49=makeQuery(id+"F3.boolean.opBoolean","SPLIT",EDGE,{"disambiguationData":[TD([makeQuery(id+"F3.opExtrude","SWEPT_FACE",FACE,{"disambiguationData":[OSD([sQuery(id+"F2.wireOp",EDGE,"E65")])]})])],"derivedFrom":makeQuery(id+"F1.opExtrude","SWEPT_EDGE",EDGE,{"disambiguationData":[OSD([subQ1,subQ0])]})});}
            var Q50;
            {var subQ0=sQuery(id+"F0.wireOp",EDGE,"E36.trimOffspring");var subQ1=sQuery(id+"F0.wireOp",EDGE,"E12");Q50=makeQuery(id+"F3.boolean.opBoolean","SPLIT",EDGE,{"disambiguationData":[TD([makeQuery(id+"F3.opExtrude","SWEPT_FACE",FACE,{"disambiguationData":[OSD([sQuery(id+"F2.wireOp",EDGE,"E65")])]})])],"derivedFrom":makeQuery(id+"F1.opExtrude","SWEPT_EDGE",EDGE,{"disambiguationData":[OSD([subQ1,subQ0])]})});}
            var Q51;
            {var subQ0=sQuery(id+"F0.wireOp",EDGE,"E36.trimOffspring");var subQ1=sQuery(id+"F0.wireOp",EDGE,"E11");Q51=makeQuery(id+"F3.boolean.opBoolean","SPLIT",EDGE,{"disambiguationData":[TD([makeQuery(id+"F3.opExtrude","SWEPT_FACE",FACE,{"disambiguationData":[OSD([sQuery(id+"F2.wireOp",EDGE,"E65")])]})])],"derivedFrom":makeQuery(id+"F1.opExtrude","SWEPT_EDGE",EDGE,{"disambiguationData":[OSD([subQ1,subQ0])]})});}
            var Q52;
            {var subQ0=sQuery(id+"F0.wireOp",EDGE,"E35.trimOffspring");var subQ1=sQuery(id+"F0.wireOp",EDGE,"E10");Q52=makeQuery(id+"F3.boolean.opBoolean","SPLIT",EDGE,{"disambiguationData":[TD([makeQuery(id+"F3.opExtrude","SWEPT_FACE",FACE,{"disambiguationData":[OSD([sQuery(id+"F2.wireOp",EDGE,"E65")])]})])],"derivedFrom":makeQuery(id+"F1.opExtrude","SWEPT_EDGE",EDGE,{"disambiguationData":[OSD([subQ1,subQ0])]})});}
            var Q53;
            {var subQ0=sQuery(id+"F0.wireOp",EDGE,"E35.trimOffspring");var subQ1=sQuery(id+"F0.wireOp",EDGE,"E9");Q53=makeQuery(id+"F3.boolean.opBoolean","SPLIT",EDGE,{"disambiguationData":[TD([makeQuery(id+"F3.opExtrude","SWEPT_FACE",FACE,{"disambiguationData":[OSD([sQuery(id+"F2.wireOp",EDGE,"E65")])]})])],"derivedFrom":makeQuery(id+"F1.opExtrude","SWEPT_EDGE",EDGE,{"disambiguationData":[OSD([subQ1,subQ0])]})});}
            var Q54;
            {var subQ0=sQuery(id+"F0.wireOp",EDGE,"E34.trimOffspring");var subQ1=sQuery(id+"F0.wireOp",EDGE,"E8");Q54=makeQuery(id+"F3.boolean.opBoolean","SPLIT",EDGE,{"disambiguationData":[TD([makeQuery(id+"F3.opExtrude","SWEPT_FACE",FACE,{"disambiguationData":[OSD([sQuery(id+"F2.wireOp",EDGE,"E65")])]})])],"derivedFrom":makeQuery(id+"F1.opExtrude","SWEPT_EDGE",EDGE,{"disambiguationData":[OSD([subQ1,subQ0])]})});}
            var Q55;
            {var subQ0=sQuery(id+"F0.wireOp",EDGE,"E34.trimOffspring");var subQ1=sQuery(id+"F0.wireOp",EDGE,"E7");Q55=makeQuery(id+"F3.boolean.opBoolean","SPLIT",EDGE,{"disambiguationData":[TD([makeQuery(id+"F3.opExtrude","SWEPT_FACE",FACE,{"disambiguationData":[OSD([sQuery(id+"F2.wireOp",EDGE,"E65")])]})])],"derivedFrom":makeQuery(id+"F1.opExtrude","SWEPT_EDGE",EDGE,{"disambiguationData":[OSD([subQ1,subQ0])]})});}
            var Q56;
            {var subQ0=sQuery(id+"F0.wireOp",EDGE,"E33.trimOffspring");var subQ1=sQuery(id+"F0.wireOp",EDGE,"E6");Q56=makeQuery(id+"F3.boolean.opBoolean","SPLIT",EDGE,{"disambiguationData":[TD([makeQuery(id+"F3.opExtrude","SWEPT_FACE",FACE,{"disambiguationData":[OSD([sQuery(id+"F2.wireOp",EDGE,"E65")])]})])],"derivedFrom":makeQuery(id+"F1.opExtrude","SWEPT_EDGE",EDGE,{"disambiguationData":[OSD([subQ1,subQ0])]})});}
            var Q57;
            {var subQ0=sQuery(id+"F0.wireOp",EDGE,"E33.trimOffspring");var subQ1=sQuery(id+"F0.wireOp",EDGE,"E5");Q57=makeQuery(id+"F3.boolean.opBoolean","SPLIT",EDGE,{"disambiguationData":[TD([makeQuery(id+"F3.opExtrude","SWEPT_FACE",FACE,{"disambiguationData":[OSD([sQuery(id+"F2.wireOp",EDGE,"E65")])]})])],"derivedFrom":makeQuery(id+"F1.opExtrude","SWEPT_EDGE",EDGE,{"disambiguationData":[OSD([subQ1,subQ0])]})});}
            var Q58;
            {var subQ0=sQuery(id+"F0.wireOp",EDGE,"E32.trimOffspring");var subQ1=sQuery(id+"F0.wireOp",EDGE,"E4");Q58=makeQuery(id+"F3.boolean.opBoolean","SPLIT",EDGE,{"disambiguationData":[TD([makeQuery(id+"F3.opExtrude","SWEPT_FACE",FACE,{"disambiguationData":[OSD([sQuery(id+"F2.wireOp",EDGE,"E65")])]})])],"derivedFrom":makeQuery(id+"F1.opExtrude","SWEPT_EDGE",EDGE,{"disambiguationData":[OSD([subQ1,subQ0])]})});}
            var Q59;
            {var subQ0=sQuery(id+"F0.wireOp",EDGE,"E32.trimOffspring");var subQ1=sQuery(id+"F0.wireOp",EDGE,"E3");Q59=makeQuery(id+"F3.boolean.opBoolean","SPLIT",EDGE,{"disambiguationData":[TD([makeQuery(id+"F3.opExtrude","SWEPT_FACE",FACE,{"disambiguationData":[OSD([sQuery(id+"F2.wireOp",EDGE,"E65")])]})])],"derivedFrom":makeQuery(id+"F1.opExtrude","SWEPT_EDGE",EDGE,{"disambiguationData":[OSD([subQ1,subQ0])]})});}
            var Q60;
            {var subQ0=sQuery(id+"F0.wireOp",EDGE,"E2");var subQ1=sQuery(id+"F0.wireOp",EDGE,"E0.top");Q60=makeQuery(id+"F3.boolean.opBoolean","SPLIT",EDGE,{"disambiguationData":[TD([makeQuery(id+"F3.opExtrude","SWEPT_FACE",FACE,{"disambiguationData":[OSD([sQuery(id+"F2.wireOp",EDGE,"E65")])]})])],"derivedFrom":makeQuery(id+"F1.opExtrude","SWEPT_EDGE",EDGE,{"disambiguationData":[OSD([subQ1,subQ0])]})});}
            chamfer(context, id + "F7", {"entities" : qUnion([Q0, Q1, Q2, Q3, Q4, Q5, Q6, Q7, Q8, Q9, Q10, Q11, Q12, Q13, Q14, Q15, Q16, Q17, Q18, Q19, Q20, Q21, Q22, Q23, Q24, Q25, Q26, Q27, Q28, Q29, Q30, Q31, Q32, Q33, Q34, Q35, Q36, Q37, Q38, Q39, Q40, Q41, Q42, Q43, Q44, Q45, Q46, Q47, Q48, Q49, Q50, Q51, Q52, Q53, Q54, Q55, Q56, Q57, Q58, Q59, Q60]), "width" : 2 * mm, "tangentPropagation" : true});
        }
    });
